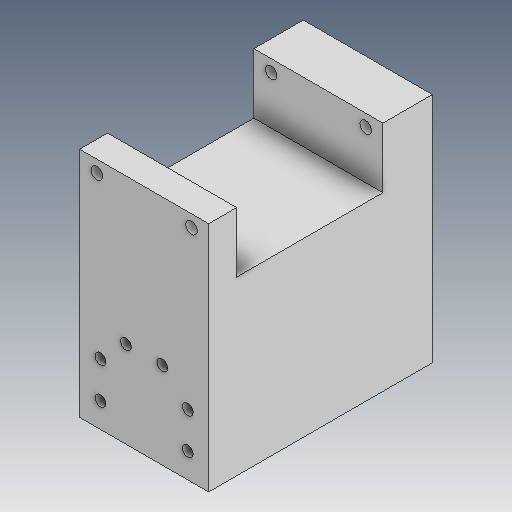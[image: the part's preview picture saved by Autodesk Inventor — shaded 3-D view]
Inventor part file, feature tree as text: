
AUTODESK INVENTOR PART (.ipt)
format: ipt  version: 2020 (Build 240168000, 168)  size: 183,296 bytes
history: native  units: mm
features: other x7, sketch x4, extrude x4, reference x4
ambient origin geometry x8: Origin, YZ Plane, XZ Plane, XY Plane, X Axis, Y Axis, Z Axis, Center Point
bodies: Body1 (feature_tree), Body2 (feature_tree)
feature tree (19):
  other  "솔리드1"
  sketch  "스케치1"
  other  "작업 평면1"
  extrude  "돌출1"  Depth=20.0mm
  sketch  "스케치2"
  other  "작업 평면2"
  extrude  "돌출2"  Depth=40.0mm
  extrude  "돌출3"  Depth=10.0mm TaperAngle=0.0deg
  extrude  "돌출4"  Depth=30.0mm
  reference  "참조1"
  reference  "참조2"
  reference  "참조3"
  sketch  "스케치3"
  sketch  "스케치4"
  reference  "참조4"
  parser-record x1  (decoder bookkeeping rows leaked as tree rows — omitted from the tree; the rows remain in map.json)
  other  "robotarm.iam"
  other  "bar2:1"
  other  "RX64_N:1"
note: 1 file-system path scrubbed to <path> (originals preserved in map.json)
